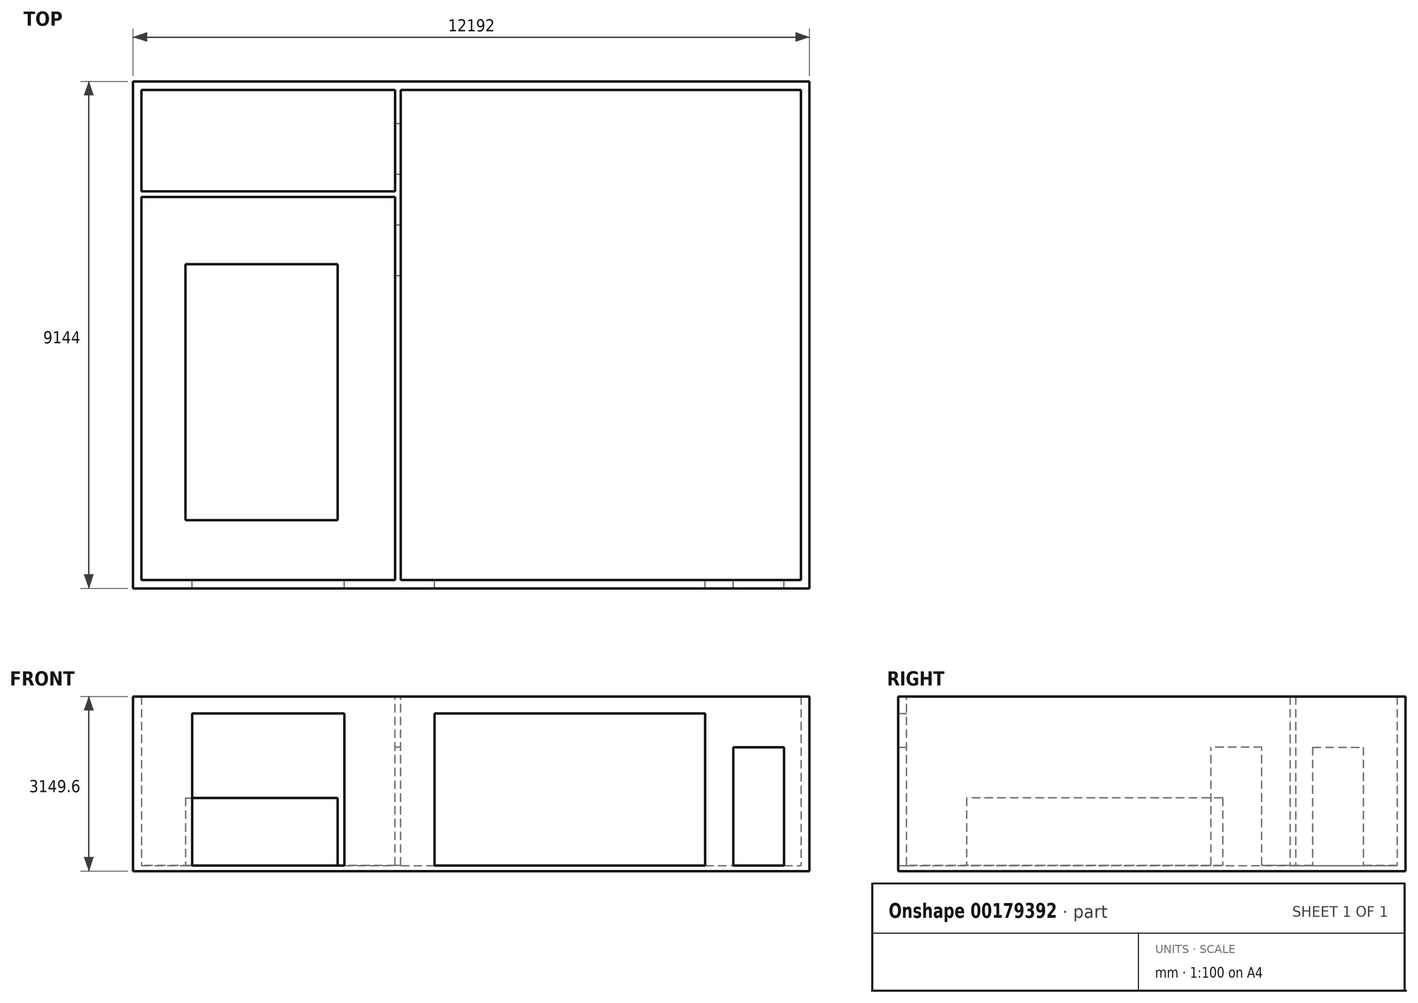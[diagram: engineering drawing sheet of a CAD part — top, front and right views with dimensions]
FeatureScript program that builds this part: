
annotation { "Feature Type Name" : "Feature", "Feature Type Description" : "" }
export const myFeature = defineFeature(function(context is Context, id is Id, definition is map)
    precondition{}
    {
        {
            var Q0;
            Q0=qCreatedBy(makeId("Top.planeOp"),FACE);
            var sketch = newSketch(context, id + "F0", { "sketchPlane" : qUnion([Q0])});
            skLineSegment(sketch, "E0.bottom", {"start": v(-9698.98, -4567.44) * mm, "end": v(2493.02, -4567.44) * mm});
            skLineSegment(sketch, "E0.top", {"start": v(-9698.98, 4576.56) * mm, "end": v(2493.02, 4576.56) * mm});
            skLineSegment(sketch, "E0.left", {"start": v(-9698.98, -4567.44) * mm, "end": v(-9698.98, 4576.56) * mm});
            skLineSegment(sketch, "E0.right", {"start": v(2493.02, -4567.44) * mm, "end": v(2493.02, 4576.56) * mm});
            skLineSegment(sketch, "E1", {"start": v(-9546.58, -4415.04) * mm, "end": v(-9546.58, 4424.16) * mm});
            skLineSegment(sketch, "E2", {"start": v(-9546.58, -4415.04) * mm, "end": v(2340.62, -4415.04) * mm});
            skLineSegment(sketch, "E3", {"start": v(2340.62, -4415.04) * mm, "end": v(2340.62, 4424.16) * mm});
            skLineSegment(sketch, "E4", {"start": v(2340.62, 4424.16) * mm, "end": v(-9546.58, 4424.16) * mm});
            skSolve(sketch);
        }
        {
            var Q0;
            Q0=makeQuery(id+"F0.imprint","IMPRINT",FACE,{"disambiguationData":[TD([[makeQuery(id+"F0.imprint","IMPRINT",EDGE,{"derivedFrom":sQuery(id+"F0.wireOp",EDGE,"E0.bottom")}),1.0]])]});
            extrude(context, id + "F1", {"entities" : qUnion([Q0]), "depth" : 3048 * mm});
        }
        {
            var Q0;
            Q0=makeQuery(id+"F1.opExtrude","SWEPT_FACE",FACE,{"disambiguationData":[OSD([sQuery(id+"F0.wireOp",EDGE,"E0.right")])]});
            var sketch = newSketch(context, id + "F2", { "sketchPlane" : qUnion([Q0])});
            skLineSegment(sketch, "E5.bottom", {"start": v(-4567.44, 0) * mm, "end": v(4576.56, 0) * mm});
            skLineSegment(sketch, "E5.top", {"start": v(-4567.44, -101.6) * mm, "end": v(4576.56, -101.6) * mm});
            skLineSegment(sketch, "E5.left", {"start": v(-4567.44, 0) * mm, "end": v(-4567.44, -101.6) * mm});
            skLineSegment(sketch, "E5.right", {"start": v(4576.56, 0) * mm, "end": v(4576.56, -101.6) * mm});
            skSolve(sketch);
        }
        {
            var Q0;
            Q0=makeQuery(id+"F2.imprint","IMPRINT",FACE,{"disambiguationData":[TD([[makeQuery(id+"F2.imprint","IMPRINT",EDGE,{"derivedFrom":sQuery(id+"F2.wireOp",EDGE,"E5.bottom")}),-1.0]])]});
            var Q1;
            Q1=makeQuery(id+"F1.opExtrude","SWEPT_FACE",FACE,{"disambiguationData":[OSD([sQuery(id+"F0.wireOp",EDGE,"E0.left")])]});
            extrude(context, id + "F3", {"entities" : qUnion([Q0]), "operationType" : NewBodyOperationType.ADD, "endBound" : BoundingType.UP_TO_SURFACE, "oppositeDirection" : true, "endBoundEntityFace" : qUnion([Q1]), "depth" : 18643.6 * mm});
        }
        {
            var Q0;
            Q0=makeQuery(id+"F1.opExtrude","SWEPT_FACE",FACE,{"disambiguationData":[OSD([sQuery(id+"F0.wireOp",EDGE,"E2")])]});
            var sketch = newSketch(context, id + "F4", { "sketchPlane" : qUnion([Q0])});
            skLineSegment(sketch, "E6.bottom", {"start": v(4872.98, 0) * mm, "end": v(4974.58, 0) * mm});
            skLineSegment(sketch, "E6.top", {"start": v(4872.98, 3048) * mm, "end": v(4974.58, 3048) * mm});
            skLineSegment(sketch, "E6.left", {"start": v(4872.98, 0) * mm, "end": v(4872.98, 3048) * mm});
            skLineSegment(sketch, "E6.right", {"start": v(4974.58, 0) * mm, "end": v(4974.58, 3048) * mm});
            skSolve(sketch);
        }
        {
            var Q0;
            Q0 = qSketchRegion(id + "F4", true);
            extrude(context, id + "F5", {"entities" : qUnion([Q0]), "operationType" : NewBodyOperationType.ADD, "endBound" : BoundingType.UP_TO_NEXT, "depth" : 25.4 * mm});
        }
        {
            var Q0;
            Q0=makeQuery(id+"F5.opExtrude","SWEPT_FACE",FACE,{"disambiguationData":[OSD([sQuery(id+"F4.wireOp",EDGE,"E6.right")])]});
            var sketch = newSketch(context, id + "F6", { "sketchPlane" : qUnion([Q0])});
            skLineSegment(sketch, "E7.bottom", {"start": v(-2595.36, 3048) * mm, "end": v(-2493.76, 3048) * mm});
            skLineSegment(sketch, "E7.top", {"start": v(-2595.36, 0) * mm, "end": v(-2493.76, 0) * mm});
            skLineSegment(sketch, "E7.left", {"start": v(-2595.36, 3048) * mm, "end": v(-2595.36, 0) * mm});
            skLineSegment(sketch, "E7.right", {"start": v(-2493.76, 3048) * mm, "end": v(-2493.76, 0) * mm});
            skSolve(sketch);
        }
        {
            var Q0;
            Q0 = qSketchRegion(id + "F6", true);
            extrude(context, id + "F7", {"entities" : qUnion([Q0]), "operationType" : NewBodyOperationType.ADD, "endBound" : BoundingType.UP_TO_NEXT, "depth" : 25.4 * mm});
        }
        {
            var Q0;
            {var subQ0=sQuery(id+"F0.wireOp",EDGE,"E1");var subQ1=sQuery(id+"F0.wireOp",EDGE,"E2");Q0=makeQuery(id+"F5.boolean.opBoolean","SPLIT",FACE,{"disambiguationData":[TD([makeQuery(id+"F1.opExtrude","SWEPT_FACE",FACE,{"disambiguationData":[OSD([subQ0])]})])],"derivedFrom":makeQuery(id+"F1.opExtrude","SWEPT_FACE",FACE,{"disambiguationData":[OSD([subQ1])]})});}
            var sketch = newSketch(context, id + "F8", { "sketchPlane" : qUnion([Q0])});
            skLineSegment(sketch, "E8.bottom", {"start": v(5888.98, 0) * mm, "end": v(8632.18, 0) * mm});
            skLineSegment(sketch, "E8.top", {"start": v(5888.98, 2743.2) * mm, "end": v(8632.18, 2743.2) * mm});
            skLineSegment(sketch, "E8.left", {"start": v(5888.98, 0) * mm, "end": v(5888.98, 2743.2) * mm});
            skLineSegment(sketch, "E8.right", {"start": v(8632.18, 0) * mm, "end": v(8632.18, 2743.2) * mm});
            skSolve(sketch);
        }
        {
            var Q0;
            Q0=makeQuery(id+"F8.imprint","IMPRINT",FACE,{"disambiguationData":[TD([[makeQuery(id+"F8.imprint","IMPRINT",EDGE,{"derivedFrom":sQuery(id+"F8.wireOp",EDGE,"E8.bottom")}),-1.0]])]});
            extrude(context, id + "F9", {"entities" : qUnion([Q0]), "operationType" : NewBodyOperationType.REMOVE, "oppositeDirection" : true, "depth" : 1574.8 * mm});
        }
        {
            var Q0;
            {var subQ0=sQuery(id+"F0.wireOp",EDGE,"E3");var subQ1=sQuery(id+"F0.wireOp",EDGE,"E2");Q0=makeQuery(id+"F5.boolean.opBoolean","SPLIT",FACE,{"disambiguationData":[TD([makeQuery(id+"F1.opExtrude","SWEPT_FACE",FACE,{"disambiguationData":[OSD([subQ0])]})])],"derivedFrom":makeQuery(id+"F1.opExtrude","SWEPT_FACE",FACE,{"disambiguationData":[OSD([subQ1])]})});}
            var sketch = newSketch(context, id + "F10", { "sketchPlane" : qUnion([Q0])});
            skLineSegment(sketch, "E9.bottom", {"start": v(4263.38, 0) * mm, "end": v(-613.42, 0) * mm});
            skLineSegment(sketch, "E9.top", {"start": v(4263.38, 2743.2) * mm, "end": v(-613.42, 2743.2) * mm});
            skLineSegment(sketch, "E9.left", {"start": v(4263.38, 0) * mm, "end": v(4263.38, 2743.2) * mm});
            skLineSegment(sketch, "E9.right", {"start": v(-613.42, 0) * mm, "end": v(-613.42, 2743.2) * mm});
            skSolve(sketch);
        }
        {
            var Q0;
            Q0=makeQuery(id+"F10.imprint","IMPRINT",FACE,{"disambiguationData":[TD([[makeQuery(id+"F10.imprint","IMPRINT",EDGE,{"derivedFrom":sQuery(id+"F10.wireOp",EDGE,"E9.bottom")}),-1.0]])]});
            extrude(context, id + "F11", {"entities" : qUnion([Q0]), "operationType" : NewBodyOperationType.REMOVE, "oppositeDirection" : true, "depth" : 3378.2 * mm});
        }
        {
            var Q0;
            {var subQ0=sQuery(id+"F0.wireOp",EDGE,"E4");Q0=makeQuery(id+"F7.boolean.opBoolean","SPLIT",FACE,{"disambiguationData":[TD([makeQuery(id+"F1.opExtrude","SWEPT_FACE",FACE,{"disambiguationData":[OSD([subQ0])]})])],"derivedFrom":makeQuery(id+"F5.opExtrude","SWEPT_FACE",FACE,{"disambiguationData":[OSD([sQuery(id+"F4.wireOp",EDGE,"E6.right")])]})});}
            var sketch = newSketch(context, id + "F12", { "sketchPlane" : qUnion([Q0])});
            skLineSegment(sketch, "E10.bottom", {"start": v(-3814.56, 0) * mm, "end": v(-2900.16, 0) * mm});
            skLineSegment(sketch, "E10.top", {"start": v(-3814.56, 2133.6) * mm, "end": v(-2900.16, 2133.6) * mm});
            skLineSegment(sketch, "E10.left", {"start": v(-3814.56, 0) * mm, "end": v(-3814.56, 2133.6) * mm});
            skLineSegment(sketch, "E10.right", {"start": v(-2900.16, 0) * mm, "end": v(-2900.16, 2133.6) * mm});
            skSolve(sketch);
        }
        {
            var Q0;
            Q0=makeQuery(id+"F12.imprint","IMPRINT",FACE,{"disambiguationData":[TD([[makeQuery(id+"F12.imprint","IMPRINT",EDGE,{"derivedFrom":sQuery(id+"F12.wireOp",EDGE,"E10.bottom")}),1.0]])]});
            extrude(context, id + "F13", {"entities" : qUnion([Q0]), "operationType" : NewBodyOperationType.REMOVE, "oppositeDirection" : true, "depth" : 1320.8 * mm});
        }
        {
            var Q0;
            Q0=makeQuery(id+"F5.opExtrude","SWEPT_FACE",FACE,{"disambiguationData":[OSD([sQuery(id+"F4.wireOp",EDGE,"E6.left")])]});
            var sketch = newSketch(context, id + "F14", { "sketchPlane" : qUnion([Q0])});
            skLineSegment(sketch, "E11.bottom", {"start": v(1986, 0) * mm, "end": v(1071.6, 0) * mm});
            skLineSegment(sketch, "E11.top", {"start": v(1986, 2133.6) * mm, "end": v(1071.6, 2133.6) * mm});
            skLineSegment(sketch, "E11.left", {"start": v(1986, 0) * mm, "end": v(1986, 2133.6) * mm});
            skLineSegment(sketch, "E11.right", {"start": v(1071.6, 0) * mm, "end": v(1071.6, 2133.6) * mm});
            skSolve(sketch);
        }
        {
            var Q0;
            Q0=makeQuery(id+"F14.imprint","IMPRINT",FACE,{"disambiguationData":[TD([[makeQuery(id+"F14.imprint","IMPRINT",EDGE,{"derivedFrom":sQuery(id+"F14.wireOp",EDGE,"E11.bottom")}),-1.0]])]});
            extrude(context, id + "F15", {"entities" : qUnion([Q0]), "operationType" : NewBodyOperationType.REMOVE, "oppositeDirection" : true, "depth" : 660.4 * mm});
        }
        {
            var Q0;
            {var subQ0=sQuery(id+"F0.wireOp",EDGE,"E3");var subQ1=sQuery(id+"F0.wireOp",EDGE,"E2");Q0=makeQuery(id+"F5.boolean.opBoolean","SPLIT",FACE,{"disambiguationData":[TD([makeQuery(id+"F1.opExtrude","SWEPT_FACE",FACE,{"disambiguationData":[OSD([subQ0])]})])],"derivedFrom":makeQuery(id+"F1.opExtrude","SWEPT_FACE",FACE,{"disambiguationData":[OSD([subQ1])]})});}
            var sketch = newSketch(context, id + "F16", { "sketchPlane" : qUnion([Q0])});
            skLineSegment(sketch, "E12.bottom", {"start": v(-2035.82, 0) * mm, "end": v(-1121.42, 0) * mm});
            skLineSegment(sketch, "E12.top", {"start": v(-2035.82, 2133.6) * mm, "end": v(-1121.42, 2133.6) * mm});
            skLineSegment(sketch, "E12.left", {"start": v(-2035.82, 0) * mm, "end": v(-2035.82, 2133.6) * mm});
            skLineSegment(sketch, "E12.right", {"start": v(-1121.42, 0) * mm, "end": v(-1121.42, 2133.6) * mm});
            skSolve(sketch);
        }
        {
            var Q0;
            Q0=makeQuery(id+"F16.imprint","IMPRINT",FACE,{"disambiguationData":[TD([[makeQuery(id+"F16.imprint","IMPRINT",EDGE,{"derivedFrom":sQuery(id+"F16.wireOp",EDGE,"E12.bottom")}),-1.0]])]});
            extrude(context, id + "F17", {"entities" : qUnion([Q0]), "operationType" : NewBodyOperationType.REMOVE, "oppositeDirection" : true, "depth" : 508 * mm});
        }
        {
            var Q0;
            {var subQ0=makeQuery(id+"F1.opExtrude","SWEPT_FACE",FACE,{"disambiguationData":[OSD([sQuery(id+"F0.wireOp",EDGE,"E2")])]});var subQ1=makeQuery(id+"F1.opExtrude","SWEPT_FACE",FACE,{"disambiguationData":[OSD([sQuery(id+"F0.wireOp",EDGE,"E4")])]});var subQ2=makeQuery(id+"F3.opExtrude","SWEPT_FACE",FACE,{"disambiguationData":[OSD([sQuery(id+"F2.wireOp",EDGE,"E5.bottom")])]});var subQ3=makeQuery(id+"F1.opExtrude","SWEPT_FACE",FACE,{"disambiguationData":[OSD([sQuery(id+"F0.wireOp",EDGE,"E1")])]});var subQ5=makeQuery(id+"F5.boolean.opBoolean","SPLIT",FACE,{"disambiguationData":[TD([subQ3])],"derivedFrom":subQ2});Q0=makeQuery(id+"F17.boolean.opBoolean","MERGE",FACE,{"derivedFrom":[makeQuery(id+"F15.boolean.opBoolean","MERGE",FACE,{"derivedFrom":[makeQuery(id+"F9.boolean.opBoolean","MERGE",FACE,{"derivedFrom":[makeQuery(id+"F7.boolean.opBoolean","SPLIT",FACE,{"disambiguationData":[TD([subQ0])],"derivedFrom":subQ5}),makeQuery(id+"F9.opExtrude","SWEPT_FACE",FACE,{"disambiguationData":[OSD([sQuery(id+"F8.wireOp",EDGE,"E8.bottom")])]})]}),makeQuery(id+"F13.boolean.opBoolean","MERGE",FACE,{"derivedFrom":[makeQuery(id+"F7.boolean.opBoolean","SPLIT",FACE,{"disambiguationData":[TD([subQ1])],"derivedFrom":subQ5}),makeQuery(id+"F11.boolean.opBoolean","MERGE",FACE,{"derivedFrom":[makeQuery(id+"F5.boolean.opBoolean","SPLIT",FACE,{"disambiguationData":[TD([makeQuery(id+"F1.opExtrude","SWEPT_FACE",FACE,{"disambiguationData":[OSD([sQuery(id+"F0.wireOp",EDGE,"E3")])]})])],"derivedFrom":subQ2}),makeQuery(id+"F11.opExtrude","SWEPT_FACE",FACE,{"disambiguationData":[OSD([sQuery(id+"F10.wireOp",EDGE,"E9.bottom")])]})]}),makeQuery(id+"F13.opExtrude","SWEPT_FACE",FACE,{"disambiguationData":[OSD([sQuery(id+"F12.wireOp",EDGE,"E10.bottom")])]})]}),makeQuery(id+"F15.opExtrude","SWEPT_FACE",FACE,{"disambiguationData":[OSD([sQuery(id+"F14.wireOp",EDGE,"E11.bottom")])]})]}),makeQuery(id+"F17.opExtrude","SWEPT_FACE",FACE,{"disambiguationData":[OSD([sQuery(id+"F16.wireOp",EDGE,"E12.bottom")])]})]});}
            var sketch = newSketch(context, id + "F18", { "sketchPlane" : qUnion([Q0])});
            skLineSegment(sketch, "E13.bottom", {"start": v(-8755.84, 1276.8) * mm, "end": v(-6012.64, 1276.8) * mm});
            skLineSegment(sketch, "E13.top", {"start": v(-8755.84, -3335.83) * mm, "end": v(-6012.64, -3335.83) * mm});
            skLineSegment(sketch, "E13.left", {"start": v(-8755.84, 1276.8) * mm, "end": v(-8755.84, -3335.83) * mm});
            skLineSegment(sketch, "E13.right", {"start": v(-6012.64, 1276.8) * mm, "end": v(-6012.64, -3335.83) * mm});
            skSolve(sketch);
        }
        {
            var Q0;
            Q0=makeQuery(id+"F18.imprint","IMPRINT",FACE,{"disambiguationData":[TD([[makeQuery(id+"F18.imprint","IMPRINT",EDGE,{"derivedFrom":sQuery(id+"F18.wireOp",EDGE,"E13.bottom")}),-1.0]])]});
            extrude(context, id + "F19", {"entities" : qUnion([Q0]), "operationType" : NewBodyOperationType.ADD, "depth" : 1219.2 * mm});
        }
    });
